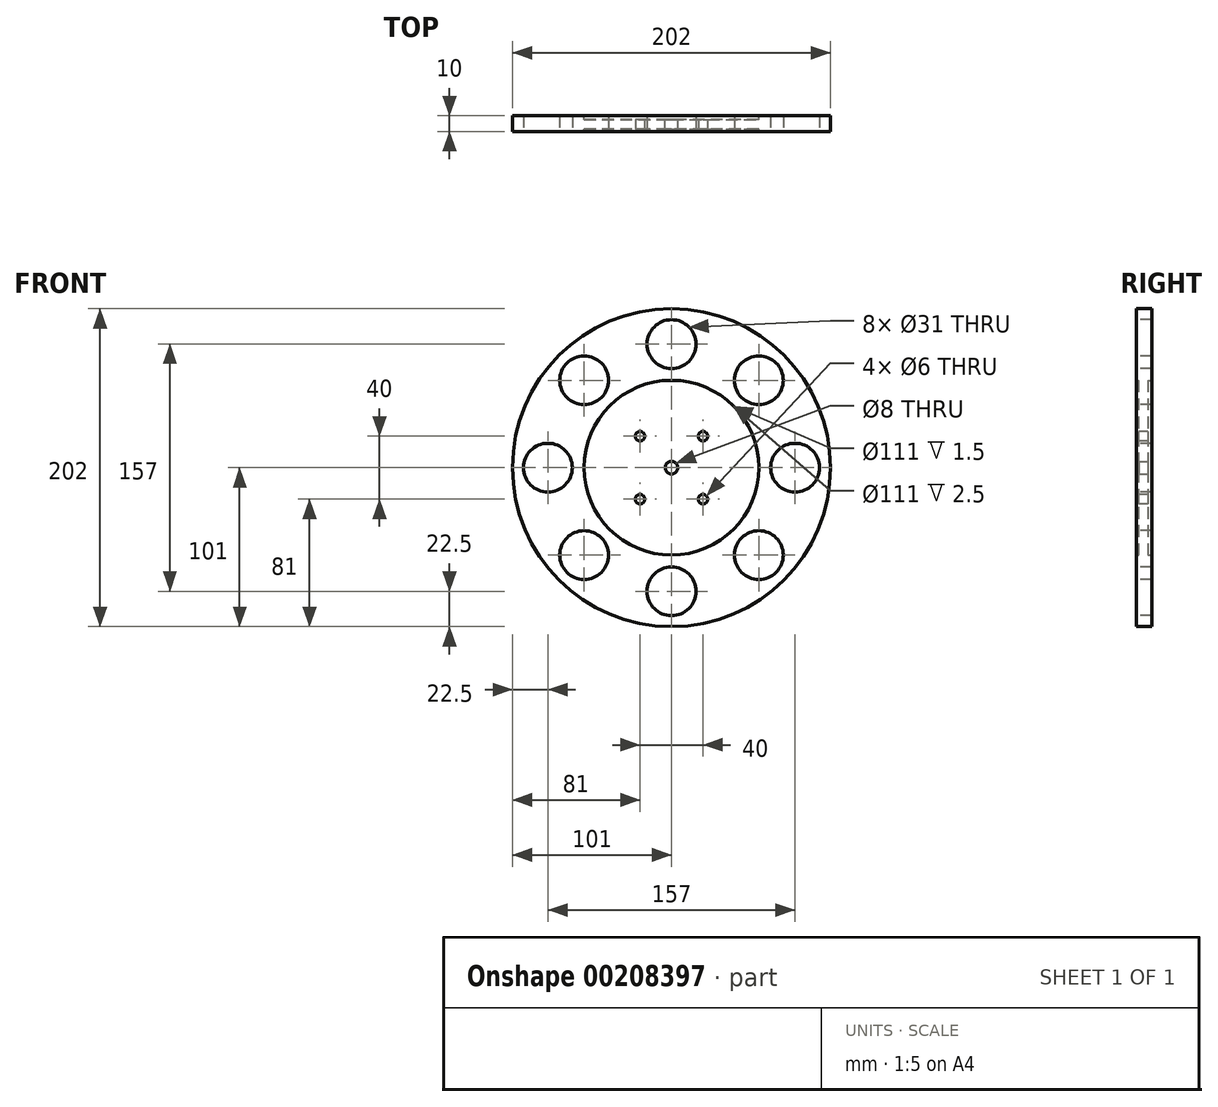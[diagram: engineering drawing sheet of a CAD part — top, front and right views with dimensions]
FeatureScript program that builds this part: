
annotation { "Feature Type Name" : "Feature", "Feature Type Description" : "" }
export const myFeature = defineFeature(function(context is Context, id is Id, definition is map)
    precondition{}
    {
        {
            var Q0;
            Q0=qCreatedBy(makeId("Front.planeOp"),FACE);
            var sketch = newSketch(context, id + "F0", { "sketchPlane" : qUnion([Q0])});
            skCircle(sketch, "E0", {"center": v(0, 0) * mm, "radius": 101 * mm});
            skCircle(sketch, "E1", {"center": v(0, 0) * mm, "radius": 4 * mm});
            skSolve(sketch);
        }
        {
            var Q0;
            Q0 = qSketchRegion(id + "F0", true);
            extrude(context, id + "F1", {"entities" : qUnion([Q0]), "depth" : 10 * mm, "symmetric" : true});
        }
        {
            var Q0;
            Q0=makeQuery(id+"F1.opExtrude","CAP_FACE",FACE,{"disambiguationData":[OSD([sQuery(id+"F0.wireOp",EDGE,"E0"),sQuery(id+"F0.wireOp",EDGE,"ctCutVhO-PMa5-CqbY-mXez-zj3eJOlwtcyv")])],"isStart":false});
            var sketch = newSketch(context, id + "F2", { "sketchPlane" : qUnion([Q0])});
            skCircle(sketch, "E2", {"center": v(0, 78.5) * mm, "radius": 15.5 * mm});
            skCircle(sketch, "E3.1.0", {"center": v(55.5, 55.5) * mm, "radius": 15.5 * mm});
            skCircle(sketch, "E3.2.0", {"center": v(78.5, 0) * mm, "radius": 15.5 * mm});
            skPoint(sketch, "E3.center", {"position": v(0, 0) * mm});
            skLineSegment(sketch, "E3.anchor1", {"start": v(0, 0) * mm, "end": v(0, 78.5) * mm, "construction": true});
            skLineSegment(sketch, "E3.anchor2", {"start": v(0, 0) * mm, "end": v(78.5, 0) * mm, "construction": true});
            skCircle(sketch, "E4.1.0", {"center": v(55.5, -55.5) * mm, "radius": 15.5 * mm});
            skCircle(sketch, "E4.2.0", {"center": v(0, -78.5) * mm, "radius": 15.5 * mm});
            skLineSegment(sketch, "E4.anchor2", {"start": v(0, 0) * mm, "end": v(0, -78.5) * mm, "construction": true});
            skCircle(sketch, "E5.1.0", {"center": v(-55.5, -55.5) * mm, "radius": 15.5 * mm});
            skCircle(sketch, "E5.2.0", {"center": v(-78.5, 0) * mm, "radius": 15.5 * mm});
            skLineSegment(sketch, "E5.anchor2", {"start": v(0, 0) * mm, "end": v(-78.5, 0) * mm, "construction": true});
            skCircle(sketch, "E6.1.0", {"center": v(-55.5, 55.5) * mm, "radius": 15.5 * mm});
            skCircle(sketch, "E7", {"center": v(-20, 20) * mm, "radius": 3 * mm});
            skCircle(sketch, "E8", {"center": v(20, 20) * mm, "radius": 3 * mm});
            skCircle(sketch, "E9", {"center": v(20, -20) * mm, "radius": 3 * mm});
            skCircle(sketch, "E10", {"center": v(-20, -20) * mm, "radius": 3 * mm});
            skSolve(sketch);
        }
        {
            var Q0;
            Q0=makeQuery(id+"F2.imprint","IMPRINT",FACE,{"disambiguationData":[TD([[makeQuery(id+"F2.imprint","IMPRINT",EDGE,{"derivedFrom":sQuery(id+"F2.wireOp",EDGE,"E5.1.0")}),1.0]])]});
            var Q1;
            Q1=makeQuery(id+"F2.imprint","IMPRINT",FACE,{"disambiguationData":[TD([[makeQuery(id+"F2.imprint","IMPRINT",EDGE,{"derivedFrom":sQuery(id+"F2.wireOp",EDGE,"E5.2.0")}),1.0]])]});
            var Q2;
            Q2=makeQuery(id+"F2.imprint","IMPRINT",FACE,{"disambiguationData":[TD([[makeQuery(id+"F2.imprint","IMPRINT",EDGE,{"derivedFrom":sQuery(id+"F2.wireOp",EDGE,"E6.1.0")}),1.0]])]});
            var Q3;
            Q3=makeQuery(id+"F2.imprint","IMPRINT",FACE,{"disambiguationData":[TD([[makeQuery(id+"F2.imprint","IMPRINT",EDGE,{"derivedFrom":sQuery(id+"F2.wireOp",EDGE,"E2")}),1.0]])]});
            var Q4;
            Q4=makeQuery(id+"F2.imprint","IMPRINT",FACE,{"disambiguationData":[TD([[makeQuery(id+"F2.imprint","IMPRINT",EDGE,{"derivedFrom":sQuery(id+"F2.wireOp",EDGE,"E3.1.0")}),1.0]])]});
            var Q5;
            Q5=makeQuery(id+"F2.imprint","IMPRINT",FACE,{"disambiguationData":[TD([[makeQuery(id+"F2.imprint","IMPRINT",EDGE,{"derivedFrom":sQuery(id+"F2.wireOp",EDGE,"E3.2.0")}),1.0]])]});
            var Q6;
            Q6=makeQuery(id+"F2.imprint","IMPRINT",FACE,{"disambiguationData":[TD([[makeQuery(id+"F2.imprint","IMPRINT",EDGE,{"derivedFrom":sQuery(id+"F2.wireOp",EDGE,"E4.1.0")}),1.0]])]});
            var Q7;
            Q7=makeQuery(id+"F2.imprint","IMPRINT",FACE,{"disambiguationData":[TD([[makeQuery(id+"F2.imprint","IMPRINT",EDGE,{"derivedFrom":sQuery(id+"F2.wireOp",EDGE,"E4.2.0")}),1.0]])]});
            var Q8;
            Q8=makeQuery(id+"F2.imprint","IMPRINT",FACE,{"disambiguationData":[TD([[makeQuery(id+"F2.imprint","IMPRINT",EDGE,{"derivedFrom":sQuery(id+"F2.wireOp",EDGE,"E7")}),1.0]])]});
            var Q9;
            Q9=makeQuery(id+"F2.imprint","IMPRINT",FACE,{"disambiguationData":[TD([[makeQuery(id+"F2.imprint","IMPRINT",EDGE,{"derivedFrom":sQuery(id+"F2.wireOp",EDGE,"E8")}),1.0]])]});
            var Q10;
            Q10=makeQuery(id+"F2.imprint","IMPRINT",FACE,{"disambiguationData":[TD([[makeQuery(id+"F2.imprint","IMPRINT",EDGE,{"derivedFrom":sQuery(id+"F2.wireOp",EDGE,"E9")}),1.0]])]});
            var Q11;
            Q11=makeQuery(id+"F2.imprint","IMPRINT",FACE,{"disambiguationData":[TD([[makeQuery(id+"F2.imprint","IMPRINT",EDGE,{"derivedFrom":sQuery(id+"F2.wireOp",EDGE,"E10")}),1.0]])]});
            var Q12;
            Q12=makeQuery(id+"F1.opExtrude","CAP_FACE",FACE,{"disambiguationData":[OSD([sQuery(id+"F0.wireOp",EDGE,"E0"),sQuery(id+"F0.wireOp",EDGE,"E1")])],"isStart":true});
            extrude(context, id + "F3", {"entities" : qUnion([Q0, Q1, Q2, Q3, Q4, Q5, Q6, Q7, Q8, Q9, Q10, Q11, Q12]), "operationType" : NewBodyOperationType.REMOVE, "endBound" : BoundingType.THROUGH_ALL, "oppositeDirection" : true, "depth" : 10 * mm});
        }
        {
            var Q0;
            Q0=makeQuery(id+"F2.imprint","IMPRINT",FACE,{"disambiguationData":[TD([[makeQuery(id+"F2.imprint","IMPRINT",EDGE,{"derivedFrom":sQuery(id+"F2.wireOp",EDGE,"E3.1.0")}),-1.0]])]});
            var sketch = newSketch(context, id + "F5", { "sketchPlane" : qUnion([Q0])});
            skCircle(sketch, "E11", {"center": v(0, 0) * mm, "radius": 55.5 * mm});
            skSolve(sketch);
        }
        {
            var Q0;
            Q0 = qSketchRegion(id + "F5", true);
            extrude(context, id + "F6", {"entities" : qUnion([Q0]), "operationType" : NewBodyOperationType.REMOVE, "depth" : 3 * mm, "symmetric" : true});
        }
        {
            var Q0;
            Q0=makeQuery(id+"F1.opExtrude","CAP_FACE",FACE,{"disambiguationData":[OSD([sQuery(id+"F0.wireOp",EDGE,"E0"),sQuery(id+"F0.wireOp",EDGE,"E1")])],"isStart":true});
            var sketch = newSketch(context, id + "F7", { "sketchPlane" : qUnion([Q0])});
            skCircle(sketch, "E12", {"center": v(0, 0) * mm, "radius": 55.5 * mm});
            skSolve(sketch);
        }
        {
            var Q0;
            Q0 = qSketchRegion(id + "F7", true);
            extrude(context, id + "F4", {"entities" : qUnion([Q0]), "operationType" : NewBodyOperationType.REMOVE, "oppositeDirection" : true, "depth" : 5 * mm, "symmetric" : true});
        }
    });
